# Revit family: Haworth_Intuity_Benching_Corner120_ThreeSided
name_source: partatom
category: Furniture Systems
revit_build: Autodesk Revit 2018 (Build: 20170223_1515(x64)
units: mm (PartAtom-declared; Revit-internal decimal feet)

## family parameters
Always vertical = Yes
Cut with Voids When Loaded = No
OmniClass Number = 23.40.70.14.64.21
OmniClass Title = Systems Furniture
Part Type = Normal
Room Calculation Point = No
Round Connector Dimension = Use Diameter
Shared = No
Work Plane-Based = No

## types (6) — shared parameters
13 in H Screen = Yes
21 in H Screen = No
Access Plate Finish = Haworth _ Paint _ Metallic Silver
Actual Height = 29 3/16"
Assembly Code = E2020200
Custom Size = No
Description = Haworth - Intuity Benching - 120 Three Pack
End Cap Offset = 1/8"
Gap Depth = 1 13/32"
J-Rail Height = 22 5/8"
Leg Height = 28"
Manufacturer = Haworth
Max. Depth = 30"
Max. Overall Depth = 63"
Max. Screen Width = 54"
Max. Width = 54"
Min. Depth = 24"
Min. Overall Depth = 51"
Min. Screen Width = 36"
Min. Width = 42"
Model = Intuity
Rail Finish = Haworth _ Paint _ Metallic Silver
Revision Number = 1
Screen Finish = Haworth _ Fabric _ Tellure _ Geranium 3A-42
Screen Mounting Height = 28 1/4"
Side Leg Offset = 1 1/4"
Size = Verify Final Dim. w/ Haworth
Standard Overall Depth = 48, 60 in.
Standard Width = 42, 48, 54 in.
Standard Worksurface Depth = 24, 30 in.
Table Thickness = 1 3/16"
URL = www.haworth.com
URL - Product = https://www.haworth.com
Utility Tray Finish = Haworth _ Paint _ Metallic Silver
Utility Tray Yes = Yes
Warranty = https://www.haworth.com
Worksurface Distance = 2 13/16"

## per-type parameters (varying)
| type | Actual Depth | Actual Overall Depth | Actual Screen Width | Actual Width | Depth | J-Rail Width | Leg Side Offset | Screen Width | Utility Tray Width | Width |
| 30d 54w | 30" | 62 13/16" | 53 3/4" | 54" | 30" | 43 3/4" | 43 3/4" | 54" | 54" | 54" |
| 30d 48w | 30" | 62 13/16" | 47 3/4" | 48" | 30" | 38 3/4" | 38 3/4" | 48" | 48" | 48" |
| 30d 42w | 30" | 62 13/16" | 41 3/4" | 42" | 30" | 33 3/4" | 33 3/4" | 42" | 42" | 42" |
| 24d 42w | 24" | 50 13/16" | 41 3/4" | 42" | 24" | 33 3/4" | 33 3/4" | 42" | 42" | 42" |
| 24d 48w | 24" | 50 13/16" | 47 3/4" | 48" | 24" | 38 3/4" | 38 3/4" | 48" | 48" | 48" |
| 24d 54w | 24" | 50 13/16" | 53 3/4" | 54" | 24" | 43 3/4" | 43 3/4" | 54" | 54" | 54" |

## geometry (parser evidence)
native form markers: Sweep x23
no freeform markers — native parametric forms only
